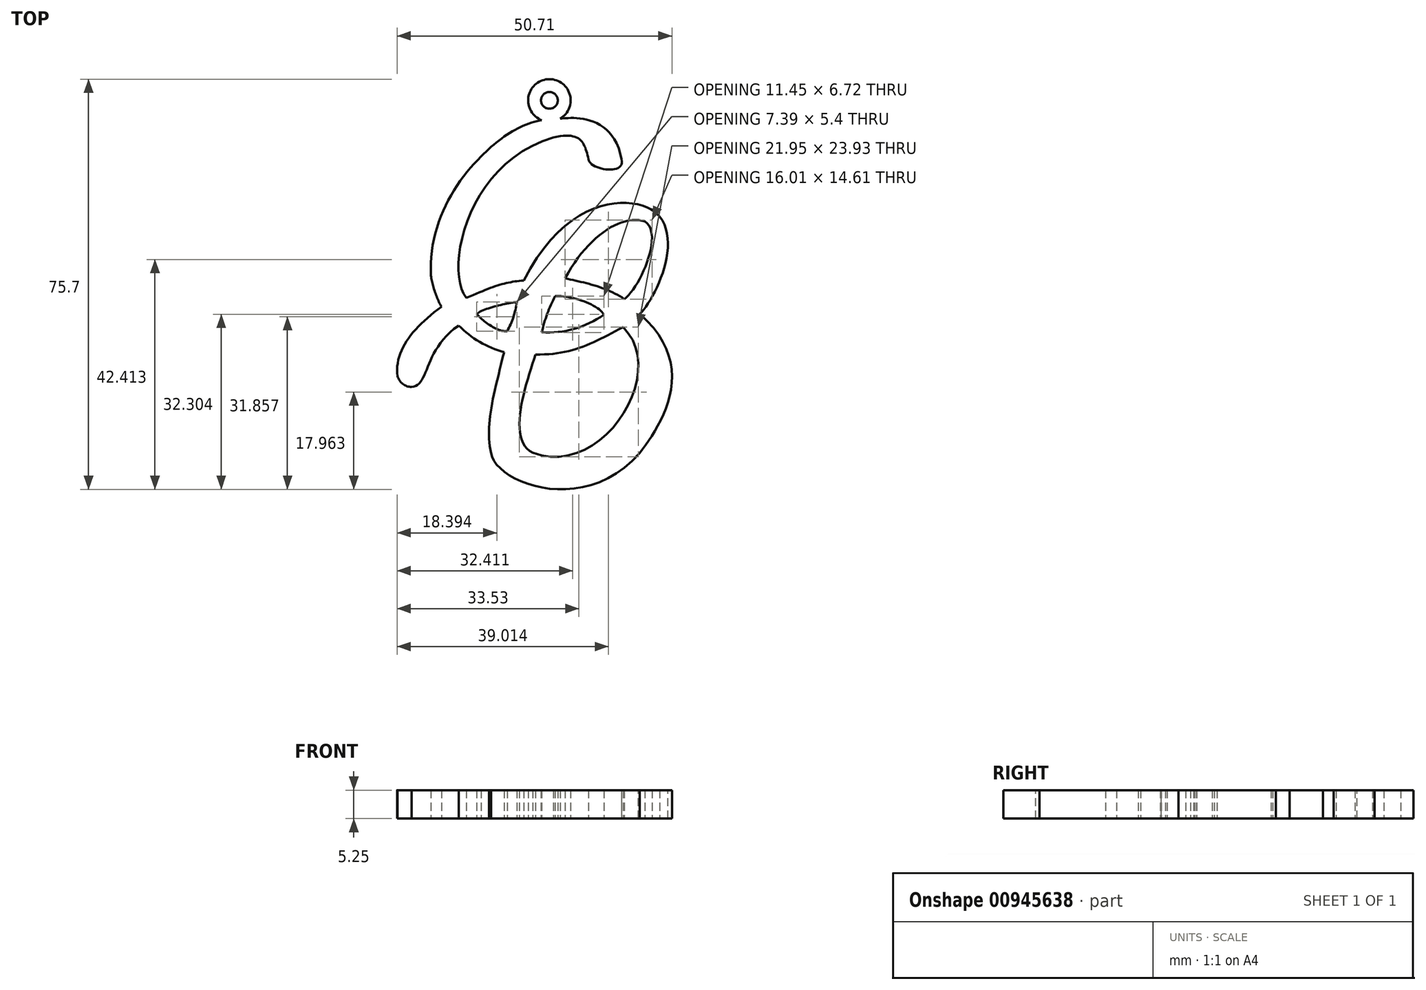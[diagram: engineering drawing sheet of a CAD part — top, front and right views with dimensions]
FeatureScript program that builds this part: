
annotation { "Feature Type Name" : "Feature", "Feature Type Description" : "" }
export const myFeature = defineFeature(function(context is Context, id is Id, definition is map)
    precondition{}
    {
        {
            var Q0;
            Q0=qCreatedBy(makeId("Top.planeOp"),FACE);
            var sketch = newSketch(context, id + "F0", { "sketchPlane" : qUnion([Q0])});
            skFitSpline(sketch, "E0", {"points": [v(-39.23, 14.7) * mm, v(-48.5, -7.3) * mm], "startDerivative": vector(-15.6, -15) * mm, "endDerivative": vector(1.78, -26.62) * mm});
            skFitSpline(sketch, "E1", {"points": [v(-13.35, 14.22) * mm, v(-19.43, 14.22) * mm], "startDerivative": vector(2.48, -9.34) * mm, "endDerivative": vector(-0.33, 5.95) * mm});
            skFitSpline(sketch, "E2", {"points": [v(-19.43, 14.22) * mm, v(-25.93, 18.18) * mm], "startDerivative": vector(-2.22, 8.87) * mm, "endDerivative": vector(-15.77, -3.77) * mm});
            skFitSpline(sketch, "E3", {"points": [v(-25.93, 18.18) * mm, v(-42, -11.4) * mm], "startDerivative": vector(-48.16, -14.02) * mm, "endDerivative": vector(12, -15.43) * mm});
            skFitSpline(sketch, "E4", {"points": [v(-42, -11.4) * mm, v(-31.37, -8.19) * mm], "startDerivative": vector(15.61, 6.7) * mm, "endDerivative": vector(10.17, 0.7) * mm});
            skFitSpline(sketch, "E5", {"points": [v(-31.37, -8.19) * mm, v(-6.3, 3.6) * mm], "startDerivative": vector(26.52, 52.66) * mm, "endDerivative": vector(8.35, -11.24) * mm});
            skFitSpline(sketch, "E6", {"points": [v(-6.3, 3.6) * mm, v(-10.02, -14.43) * mm], "startDerivative": vector(12.35, -15.67) * mm, "endDerivative": vector(-7.92, -7.63) * mm});
            skFitSpline(sketch, "E7", {"points": [v(-23.74, -7.79) * mm, v(-9.05, 2.7) * mm], "startDerivative": vector(12.5, 23.6) * mm, "endDerivative": vector(12.4, -4.4) * mm});
            skFitSpline(sketch, "E8", {"points": [v(-9.05, 2.7) * mm, v(-12.84, -11.62) * mm], "startDerivative": vector(10.6, -6.35) * mm, "endDerivative": vector(-8.96, -6.61) * mm});
            skFitSpline(sketch, "E9", {"points": [v(-23.74, -7.79) * mm, v(-12.84, -11.62) * mm], "startDerivative": vector(10.58, -2.31) * mm, "endDerivative": vector(9.23, -6.6) * mm});
            skFitSpline(sketch, "E10", {"points": [v(-40.05, -14.35) * mm, v(-32.66, -12.17) * mm], "startDerivative": vector(3.54, 3.13) * mm, "endDerivative": vector(5.65, 0.47) * mm});
            skArc(sketch, "E11", {"start": v(-34.45, -17.57) * mm, "mid": v(-33.3, -14.95) * mm, "end": v(-32.66, -12.17) * mm});
            skArc(sketch, "E12", {"start": v(-28.06, -17.76) * mm, "mid": v(-22.06, -17.1) * mm, "end": v(-16.62, -14.51) * mm});
            skArc(sketch, "E13", {"start": v(-25.6, -11.07) * mm, "mid": v(-27.05, -14.33) * mm, "end": v(-28.06, -17.76) * mm});
            skFitSpline(sketch, "E14", {"points": [v(-25.6, -11.07) * mm, v(-16.62, -14.51) * mm], "startDerivative": vector(7.6, 0.62) * mm, "endDerivative": vector(2.92, -6.03) * mm});
            skFitSpline(sketch, "E15", {"points": [v(-48.5, -7.3) * mm, v(-46.6, -13.06) * mm], "startDerivative": vector(0.56, -5.34) * mm, "endDerivative": vector(2.62, -5.01) * mm});
            skFitSpline(sketch, "E16", {"points": [v(-46.6, -13.06) * mm, v(-54.68, -25.85) * mm], "startDerivative": vector(-15.79, -11.56) * mm, "endDerivative": vector(1.95, -14.15) * mm});
            skArc(sketch, "E17", {"start": v(-54.68, -25.85) * mm, "mid": v(-53.73, -27.27) * mm, "end": v(-52.11, -27.84) * mm});
            skFitSpline(sketch, "E18", {"points": [v(-52.11, -27.84) * mm, v(-43.41, -16.5) * mm], "startDerivative": vector(10.34, 1) * mm, "endDerivative": vector(20.13, 14.15) * mm});
            skArc(sketch, "E19", {"start": v(-43.41, -16.5) * mm, "mid": v(-39.54, -19.5) * mm, "end": v(-35.02, -21.38) * mm});
            skFitSpline(sketch, "E20", {"points": [v(-29.21, -21.83) * mm, v(-13.06, -16.8) * mm], "startDerivative": vector(19.58, -0.44) * mm, "endDerivative": vector(16.83, 9) * mm});
            skFitSpline(sketch, "E21", {"points": [v(-29.75, -39.98) * mm, v(-13.06, -16.8) * mm], "startDerivative": vector(38.18, -14.64) * mm, "endDerivative": vector(-25.84, 25.08) * mm});
            skFitSpline(sketch, "E22", {"points": [v(-29.75, -39.98) * mm, v(-29.21, -21.83) * mm], "startDerivative": vector(-14, 6.93) * mm, "endDerivative": vector(6.38, 19.3) * mm});
            skFitSpline(sketch, "E23", {"points": [v(-9.98, -14.4) * mm, v(-9.98, -40.04) * mm], "startDerivative": vector(33.58, -28.83) * mm, "endDerivative": vector(-11.51, -15.27) * mm});
            skFitSpline(sketch, "E24", {"points": [v(-9.98, -40.04) * mm, v(-37.44, -40.04) * mm], "startDerivative": vector(-31.33, -35.72) * mm, "endDerivative": vector(-2.41, 16.04) * mm});
            skFitSpline(sketch, "E25", {"points": [v(-35.02, -21.38) * mm, v(-37.44, -40.04) * mm], "startDerivative": vector(-6.38, -26.04) * mm, "endDerivative": vector(3.3, -15.16) * mm});
            skCircle(sketch, "E26", {"center": v(-26.66, 25.06) * mm, "radius": 1.54 * mm});
            skArc(sketch, "E27", {"start": v(-24.68, 21.68) * mm, "mid": v(-26.98, 28.96) * mm, "end": v(-28.06, 21.4) * mm});
            skFitSpline(sketch, "E28", {"points": [v(-39.23, 14.7) * mm, v(-28.06, 21.4) * mm], "startDerivative": vector(10.24, 10.73) * mm, "endDerivative": vector(11.04, 1.76) * mm});
            skFitSpline(sketch, "E29", {"points": [v(-24.68, 21.68) * mm, v(-13.35, 14.22) * mm], "startDerivative": vector(5.8, 0.63) * mm, "endDerivative": vector(4.55, -25.65) * mm});
            skFitSpline(sketch, "E30", {"points": [v(-40.05, -14.35) * mm, v(-34.45, -17.57) * mm], "startDerivative": vector(3.48, -4.13) * mm, "endDerivative": vector(5.6, 0.27) * mm});
            skSolve(sketch);
        }
        {
            var Q0;
            Q0 = qSketchRegion(id + "F0", true);
            extrude(context, id + "F1", {"entities" : qUnion([Q0]), "depth" : 5.25 * mm, "offsetDistance" : 25 * mm});
        }
    });
